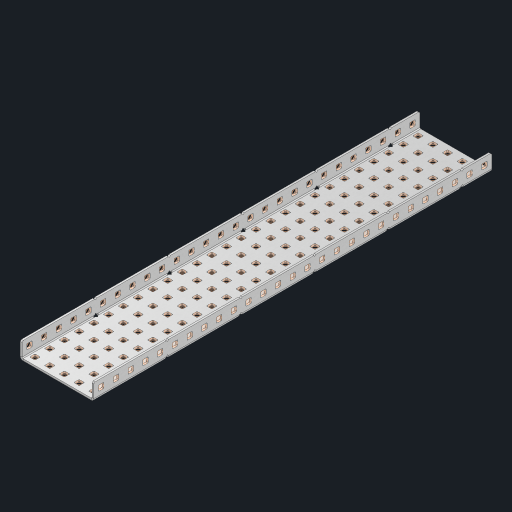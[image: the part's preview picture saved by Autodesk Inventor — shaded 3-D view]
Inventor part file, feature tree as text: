
AUTODESK INVENTOR PART (.ipt)
format: ipt  version: 2023 (Build 270158000, 158)  size: 2,101,248 bytes
history: native  units: in
note: dims shown in document units (in); Inventor stores cm internally (conversion verified against a paired STEP export)
features: other x194, extrude x188, sheet_metal_op x10, sketch x8, mirror x1, pattern_linear x1, chamfer x1
ambient origin geometry x8: Origin, YZ Plane, XZ Plane, XY Plane, X Axis, Y Axis, Z Axis, Center Point
bodies: Solid1 (feature_tree), Body (feature_tree)
feature tree (403):
  other  "Flange Pattern Plane"
  sheet_metal_op  "Flange Pattern"
  sheet_metal_op  "Body Pattern"
  other  "Arc Length"
  mirror  "Notch Mirror"
  pattern_linear  "Notch Pattern"  Spacing1=0.25in  [1 undecoded]
  chamfer  "End Chamfer"
  extrude  "Half Cut"  Depth=0.0625in
  sketch  "Sketch1"  dims[d0=2.5in]
  other  "Plate1"
  sketch  "Sketch2"  dims[d1=13.5in]
  other  "Plate2"
  sheet_metal_op  "Bend1"
  sheet_metal_op  "Corner1"
  sketch  "Sketch3"  dims[d2=0.0625in]
  other  "Flange Pattern Sketch"
  sketch  "Sketch7"  dims[d3=0.0625in]
  other  "Srf1"
  other  "Srf2"
  sketch  "Sketch8"  dims[d4=0.0312in]
  sketch  "Sketch9"  dims[d5=0.125in]
  other  "Srf91"
  sheet_metal_op  "Body Pattern Sketch"
  other  "Srf92"
  sketch  "Sketch13"  dims[d6=0.0625in]
  sketch  "Sketch14"  dims[d7=0.5in d8=90.0deg d9=0.0312in d10=0.25in d11=0.0625in d12=0.0625in d16=0.182in d17=0.02in d18=0.0625in d19=0.0in d20=0.25in d21=0.25in d46=0.172in d47=1.0in d48=0.0in d49=0.182in d50=0.02in d51=0.25in d52=0.25in d53=0.0625in d54=0.0in d55=0.172in d56=1.0in d57=0.0in d60=10.6299in d62=0.5in d63=1.9685in d65=0.5in d85=0.1473in d86=0.1782in d88=0.04in d89=0.0625in d90=0.0in d91=0.04in d92=0.0491in d95=2.5in d96=0.04in d97=0.25in d98=45.0deg d101=0.0in d102=2.497in d131=2.5in d132=10.6299in d134=0.5in d139=0.5in]
  other  "Srf856"
  other  "Srf1310"
  other  "Srf1311"
  other  "Srf1312"
  other  "Srf1376"
  other  "Srf1377"
  other  "Srf1728"
  other  "Srf1755"
  other  "Srf1878"
  other  "Srf1879"
  other  "Srf1880"
  other  "Srf1881"
  other  "Srf1882"
  other  "Srf1883"
  other  "Srf1884"
  other  "Srf1885"
  other  "Srf1886"
  other  "Srf1887"
  other  "Srf1888"
  other  "Srf1889"
  other  "Srf1890"
  other  "Srf1891"
  other  "Srf1892"
  other  "Srf1893"
  other  "Srf1894"
  other  "Srf1895"
  other  "Srf1896"
  other  "Srf1897"
  other  "Srf1898"
  other  "Srf1899"
  other  "Srf1900"
  other  "Srf1901"
  other  "Srf1902"
  other  "Srf1903"
  other  "Srf1904"
  other  "Srf1905"
  other  "Srf1906"
  other  "Srf1942"
  other  "Srf1943"
  other  "Srf1944"
  other  "Srf1945"
  other  "Srf1946"
  other  "Srf1947"
  other  "Srf1948"
  other  "Srf1949"
  other  "Srf1950"
  other  "Srf1951"
  other  "Srf1952"
  other  "Srf1953"
  other  "Srf1954"
  other  "Srf1955"
  other  "Srf1956"
  other  "Srf1957"
  other  "Srf1958"
  other  "Srf1959"
  other  "Srf1960"
  other  "Srf1961"
  other  "Srf1962"
  other  "Srf1963"
  other  "Srf1964"
  other  "Srf1965"
  other  "Srf1966"
  other  "Srf1967"
  other  "Srf1968"
  other  "Srf1969"
  other  "Srf1970"
  other  "Srf2111"
  other  "Srf2112"
  other  "Srf2113"
  other  "Srf2114"
  other  "Srf2115"
  other  "Srf2116"
  other  "Srf2117"
  other  "Srf2118"
  other  "Srf2119"
  other  "Srf2120"
  other  "Srf2121"
  other  "Srf2122"
  other  "Srf2123"
  other  "Srf2124"
  other  "Srf2125"
  other  "Srf2126"
  other  "Srf2127"
  other  "Srf2128"
  other  "Srf2129"
  other  "Srf2146"
  other  "Srf2147"
  other  "Srf2148"
  other  "Srf2149"
  other  "Srf2150"
  other  "Srf2151"
  other  "Srf2152"
  other  "Srf2153"
  other  "Srf2154"
  other  "Srf2155"
  other  "Srf2156"
  other  "Srf2157"
  other  "Srf2158"
  other  "Srf2159"
  other  "Srf2160"
  other  "Srf2161"
  other  "Srf2162"
  other  "Srf2163"
  other  "Srf2164"
  other  "Srf2165"
  other  "Srf2166"
  other  "Srf2167"
  other  "Srf2168"
  other  "Srf2169"
  other  "Srf2170"
  other  "Srf2171"
  other  "Srf2172"
  other  "Srf2173"
  other  "Srf2174"
  other  "Srf2175"
  other  "Srf2176"
  other  "Srf2177"
  other  "Srf2178"
  other  "Srf2179"
  other  "Srf2180"
  other  "Srf2181"
  other  "Srf2182"
  other  "Srf2183"
  other  "Srf2184"
  other  "Srf2185"
  other  "Srf2186"
  other  "Srf2187"
  other  "Srf2188"
  other  "Srf2189"
  other  "Srf2190"
  other  "Srf2191"
  other  "Srf2192"
  other  "Srf2193"
  other  "Srf2194"
  other  "Srf2195"
  other  "Srf2196"
  other  "Srf2197"
  other  "Srf2198"
  other  "Srf2199"
  other  "Srf2200"
  other  "Srf2201"
  other  "Srf2202"
  other  "Srf2203"
  other  "Srf2204"
  other  "Srf2205"
  other  "Srf2206"
  other  "Srf2207"
  other  "Srf2208"
  other  "Srf2209"
  other  "Srf2210"
  other  "Srf2211"
  other  "Srf2212"
  other  "Srf2213"
  other  "Srf2214"
  other  "Srf2215"
  other  "Srf2216"
  other  "Srf2217"
  other  "Srf2218"
  other  "Srf2219"
  other  "Srf2220"
  other  "Srf2221"
  other  "Srf2222"
  other  "Srf2223"
  other  "Srf2224"
  other  "Srf2225"
  other  "Srf2226"
  other  "Srf2227"
  other  "Srf2228"
  other  "Srf2229"
  other  "Srf2230"
  other  "Srf2231"
  other  "Srf2232"
  other  "Srf2233"
  other  "Srf2234"
  other  "Srf2235"
  other  "Srf2236"
  other  "Srf2237"
  other  "Srf2238"
  other  "Srf2239"
  other  "Srf2240"
  other  "Srf2241"
  other  "Srf2242"
  other  "Srf2243"
  other  "Srf2244"
  other  "Srf2245"
  sheet_metal_op  "Flange Stamp"
  sheet_metal_op  "Flange Circle"
  sheet_metal_op  "Body Stamp"
  sheet_metal_op  "Body Circle"
  sheet_metal_op  "Notch"
  extrude  "ExtrusionSrf2"  Depth=0.0625in
  extrude  "ExtrusionSrf92"  Depth=2.5in
  extrude  "ExtrusionSrf856"  Depth=0.02in
  extrude  "ExtrusionSrf1310"  Depth=0.0625in
  extrude  "ExtrusionSrf1311"  TaperAngle=0.0deg  [1 undecoded]
  extrude  "ExtrusionSrf1312"  Depth=0.25in
  extrude  "ExtrusionSrf1376"  Depth=0.25in
  extrude  "ExtrusionSrf1377"  Depth=2.5in
  extrude  "ExtrusionSrf1728"  Depth=2.5in TaperAngle=0.0deg
  extrude  "ExtrusionSrf1755"  Depth=2.5in
  extrude  "ExtrusionSrf1878"  Depth=0.02in
  extrude  "ExtrusionSrf1879"  Depth=0.25in
  extrude  "ExtrusionSrf1880"  Depth=0.25in
  extrude  "ExtrusionSrf1881"  Depth=0.0625in
  extrude  "ExtrusionSrf1882"  TaperAngle=0.0deg  [1 undecoded]
  extrude  "ExtrusionSrf1883"  Depth=2.5in
  extrude  "ExtrusionSrf1884"  Depth=2.5in TaperAngle=0.0deg
  extrude  "ExtrusionSrf1885"  Depth=2.5in
  extrude  "ExtrusionSrf1886"  Depth=2.5in
  extrude  "ExtrusionSrf1887"  Depth=2.5in
  extrude  "ExtrusionSrf1888"  Depth=2.5in
  extrude  "ExtrusionSrf1889"  Depth=2.5in
  extrude  "ExtrusionSrf1890"  Depth=0.0625in
  extrude  "ExtrusionSrf1891"  TaperAngle=0.0deg  [1 undecoded]
  extrude  "ExtrusionSrf1892"  Depth=2.5in
  extrude  "ExtrusionSrf1893"  Depth=2.5in
  extrude  "ExtrusionSrf1894"  Depth=2.5in
  extrude  "ExtrusionSrf1895"  Depth=0.25in TaperAngle=45.0deg
  extrude  "ExtrusionSrf1896"  TaperAngle=0.0deg  [1 undecoded]
  extrude  "ExtrusionSrf1897"  Depth=2.5in
  extrude  "ExtrusionSrf1898"  Depth=2.5in
  extrude  "ExtrusionSrf1899"  Depth=2.5in
  extrude  "ExtrusionSrf1900"  Depth=2.5in
  extrude  "ExtrusionSrf1901"  Depth=2.5in
  extrude  "ExtrusionSrf1902"  [1 undecoded]
  extrude  "ExtrusionSrf1903"  [1 undecoded]
  extrude  "ExtrusionSrf1904"  [1 undecoded]
  extrude  "ExtrusionSrf1905"  [1 undecoded]
  extrude  "ExtrusionSrf1906"  [1 undecoded]
  extrude  "ExtrusionSrf1942"  [1 undecoded]
  extrude  "ExtrusionSrf1943"  [1 undecoded]
  extrude  "ExtrusionSrf1944"  [1 undecoded]
  extrude  "ExtrusionSrf1945"  [1 undecoded]
  extrude  "ExtrusionSrf1946"  [1 undecoded]
  extrude  "ExtrusionSrf1947"  [1 undecoded]
  extrude  "ExtrusionSrf1948"  [1 undecoded]
  extrude  "ExtrusionSrf1949"  [1 undecoded]
  extrude  "ExtrusionSrf1950"  [1 undecoded]
  extrude  "ExtrusionSrf1951"  [1 undecoded]
  extrude  "ExtrusionSrf1952"  [1 undecoded]
  extrude  "ExtrusionSrf1953"  [1 undecoded]
  extrude  "ExtrusionSrf1954"  [1 undecoded]
  extrude  "ExtrusionSrf1955"  [1 undecoded]
  extrude  "ExtrusionSrf1956"  [1 undecoded]
  extrude  "ExtrusionSrf1957"  [1 undecoded]
  extrude  "ExtrusionSrf1958"  [1 undecoded]
  extrude  "ExtrusionSrf1959"  [1 undecoded]
  extrude  "ExtrusionSrf1960"  [1 undecoded]
  extrude  "ExtrusionSrf1961"  [1 undecoded]
  extrude  "ExtrusionSrf1962"  [1 undecoded]
  extrude  "ExtrusionSrf1963"  [1 undecoded]
  extrude  "ExtrusionSrf1964"  [1 undecoded]
  extrude  "ExtrusionSrf1965"  [1 undecoded]
  extrude  "ExtrusionSrf1966"  [1 undecoded]
  extrude  "ExtrusionSrf1967"  [1 undecoded]
  extrude  "ExtrusionSrf1968"  [1 undecoded]
  extrude  "ExtrusionSrf1969"  [1 undecoded]
  extrude  "ExtrusionSrf1970"  [1 undecoded]
  extrude  "ExtrusionSrf2111"  [1 undecoded]
  extrude  "ExtrusionSrf2112"  [1 undecoded]
  extrude  "ExtrusionSrf2113"  [1 undecoded]
  extrude  "ExtrusionSrf2114"  [1 undecoded]
  extrude  "ExtrusionSrf2115"  [1 undecoded]
  extrude  "ExtrusionSrf2116"  [1 undecoded]
  extrude  "ExtrusionSrf2117"  [1 undecoded]
  extrude  "ExtrusionSrf2118"  [1 undecoded]
  extrude  "ExtrusionSrf2119"  [1 undecoded]
  extrude  "ExtrusionSrf2120"  [1 undecoded]
  extrude  "ExtrusionSrf2121"  [1 undecoded]
  extrude  "ExtrusionSrf2122"  [1 undecoded]
  extrude  "ExtrusionSrf2123"  [1 undecoded]
  extrude  "ExtrusionSrf2124"  [1 undecoded]
  extrude  "ExtrusionSrf2125"  [1 undecoded]
  extrude  "ExtrusionSrf2126"  [1 undecoded]
  extrude  "ExtrusionSrf2127"  [1 undecoded]
  extrude  "ExtrusionSrf2128"  [1 undecoded]
  extrude  "ExtrusionSrf2129"  [1 undecoded]
  extrude  "ExtrusionSrf2146"  [1 undecoded]
  extrude  "ExtrusionSrf2147"  [1 undecoded]
  extrude  "ExtrusionSrf2148"  [1 undecoded]
  extrude  "ExtrusionSrf2149"  [1 undecoded]
  extrude  "ExtrusionSrf2150"  [1 undecoded]
  extrude  "ExtrusionSrf2151"  [1 undecoded]
  extrude  "ExtrusionSrf2152"  [1 undecoded]
  extrude  "ExtrusionSrf2153"  [1 undecoded]
  extrude  "ExtrusionSrf2154"  [1 undecoded]
  extrude  "ExtrusionSrf2155"  [1 undecoded]
  extrude  "ExtrusionSrf2156"  [1 undecoded]
  extrude  "ExtrusionSrf2157"  [1 undecoded]
  extrude  "ExtrusionSrf2158"  [1 undecoded]
  extrude  "ExtrusionSrf2159"  [1 undecoded]
  extrude  "ExtrusionSrf2160"  [1 undecoded]
  extrude  "ExtrusionSrf2161"  [1 undecoded]
  extrude  "ExtrusionSrf2162"  [1 undecoded]
  extrude  "ExtrusionSrf2163"  [1 undecoded]
  extrude  "ExtrusionSrf2164"  [1 undecoded]
  extrude  "ExtrusionSrf2165"  [1 undecoded]
  extrude  "ExtrusionSrf2166"  [1 undecoded]
  extrude  "ExtrusionSrf2167"  [1 undecoded]
  extrude  "ExtrusionSrf2168"  [1 undecoded]
  extrude  "ExtrusionSrf2169"  [1 undecoded]
  extrude  "ExtrusionSrf2170"  [1 undecoded]
  extrude  "ExtrusionSrf2171"  [1 undecoded]
  extrude  "ExtrusionSrf2172"  [1 undecoded]
  extrude  "ExtrusionSrf2173"  [1 undecoded]
  extrude  "ExtrusionSrf2174"  [1 undecoded]
  extrude  "ExtrusionSrf2175"  [1 undecoded]
  extrude  "ExtrusionSrf2176"  [1 undecoded]
  extrude  "ExtrusionSrf2177"  [1 undecoded]
  extrude  "ExtrusionSrf2178"  [1 undecoded]
  extrude  "ExtrusionSrf2179"  [1 undecoded]
  extrude  "ExtrusionSrf2180"  [1 undecoded]
  extrude  "ExtrusionSrf2181"  [1 undecoded]
  extrude  "ExtrusionSrf2182"  [1 undecoded]
  extrude  "ExtrusionSrf2183"  [1 undecoded]
  extrude  "ExtrusionSrf2184"  [1 undecoded]
  extrude  "ExtrusionSrf2185"  [1 undecoded]
  extrude  "ExtrusionSrf2186"  [1 undecoded]
  extrude  "ExtrusionSrf2187"  [1 undecoded]
  extrude  "ExtrusionSrf2188"  [1 undecoded]
  extrude  "ExtrusionSrf2189"  [1 undecoded]
  extrude  "ExtrusionSrf2190"  [1 undecoded]
  extrude  "ExtrusionSrf2191"  [1 undecoded]
  extrude  "ExtrusionSrf2192"  [1 undecoded]
  extrude  "ExtrusionSrf2193"  [1 undecoded]
  extrude  "ExtrusionSrf2194"  [1 undecoded]
  extrude  "ExtrusionSrf2195"  [1 undecoded]
  extrude  "ExtrusionSrf2196"  [1 undecoded]
  extrude  "ExtrusionSrf2197"  [1 undecoded]
  extrude  "ExtrusionSrf2198"  [1 undecoded]
  extrude  "ExtrusionSrf2199"  [1 undecoded]
  extrude  "ExtrusionSrf2200"  [1 undecoded]
  extrude  "ExtrusionSrf2201"  [1 undecoded]
  extrude  "ExtrusionSrf2202"  [1 undecoded]
  extrude  "ExtrusionSrf2203"  [1 undecoded]
  extrude  "ExtrusionSrf2204"  [1 undecoded]
  extrude  "ExtrusionSrf2205"  [1 undecoded]
  extrude  "ExtrusionSrf2206"  [1 undecoded]
  extrude  "ExtrusionSrf2207"  [1 undecoded]
  extrude  "ExtrusionSrf2208"  [1 undecoded]
  extrude  "ExtrusionSrf2209"  [1 undecoded]
  extrude  "ExtrusionSrf2210"  [1 undecoded]
  extrude  "ExtrusionSrf2211"  [1 undecoded]
  extrude  "ExtrusionSrf2212"  [1 undecoded]
  extrude  "ExtrusionSrf2213"  [1 undecoded]
  extrude  "ExtrusionSrf2214"  [1 undecoded]
  extrude  "ExtrusionSrf2215"  [1 undecoded]
  extrude  "ExtrusionSrf2216"  [1 undecoded]
  extrude  "ExtrusionSrf2217"  [1 undecoded]
  extrude  "ExtrusionSrf2218"  [1 undecoded]
  extrude  "ExtrusionSrf2219"  [1 undecoded]
  extrude  "ExtrusionSrf2220"  [1 undecoded]
  extrude  "ExtrusionSrf2221"  [1 undecoded]
  extrude  "ExtrusionSrf2222"  [1 undecoded]
  extrude  "ExtrusionSrf2223"  [1 undecoded]
  extrude  "ExtrusionSrf2224"  [1 undecoded]
  extrude  "ExtrusionSrf2225"  [1 undecoded]
  extrude  "ExtrusionSrf2226"  [1 undecoded]
  extrude  "ExtrusionSrf2227"  [1 undecoded]
  extrude  "ExtrusionSrf2228"  [1 undecoded]
  extrude  "ExtrusionSrf2229"  [1 undecoded]
  extrude  "ExtrusionSrf2230"  [1 undecoded]
  extrude  "ExtrusionSrf2231"  [1 undecoded]
  extrude  "ExtrusionSrf2232"  [1 undecoded]
  extrude  "ExtrusionSrf2233"  [1 undecoded]
  extrude  "ExtrusionSrf2234"  [1 undecoded]
  extrude  "ExtrusionSrf2235"  [1 undecoded]
  extrude  "ExtrusionSrf2236"  [1 undecoded]
  extrude  "ExtrusionSrf2237"  [1 undecoded]
  extrude  "ExtrusionSrf2238"  [1 undecoded]
  extrude  "ExtrusionSrf2239"  [1 undecoded]
  extrude  "ExtrusionSrf2240"  [1 undecoded]
  extrude  "ExtrusionSrf2241"  [1 undecoded]
  extrude  "ExtrusionSrf2242"  [1 undecoded]
  extrude  "ExtrusionSrf2243"  [1 undecoded]
  extrude  "ExtrusionSrf2244"  [1 undecoded]
  extrude  "ExtrusionSrf2245"  [1 undecoded]
note: 158 required parameter values undecoded (feature->parameter linkage not recoverable at this tier; creation-order binding heuristic only, values carry confidence <= 0.55)
